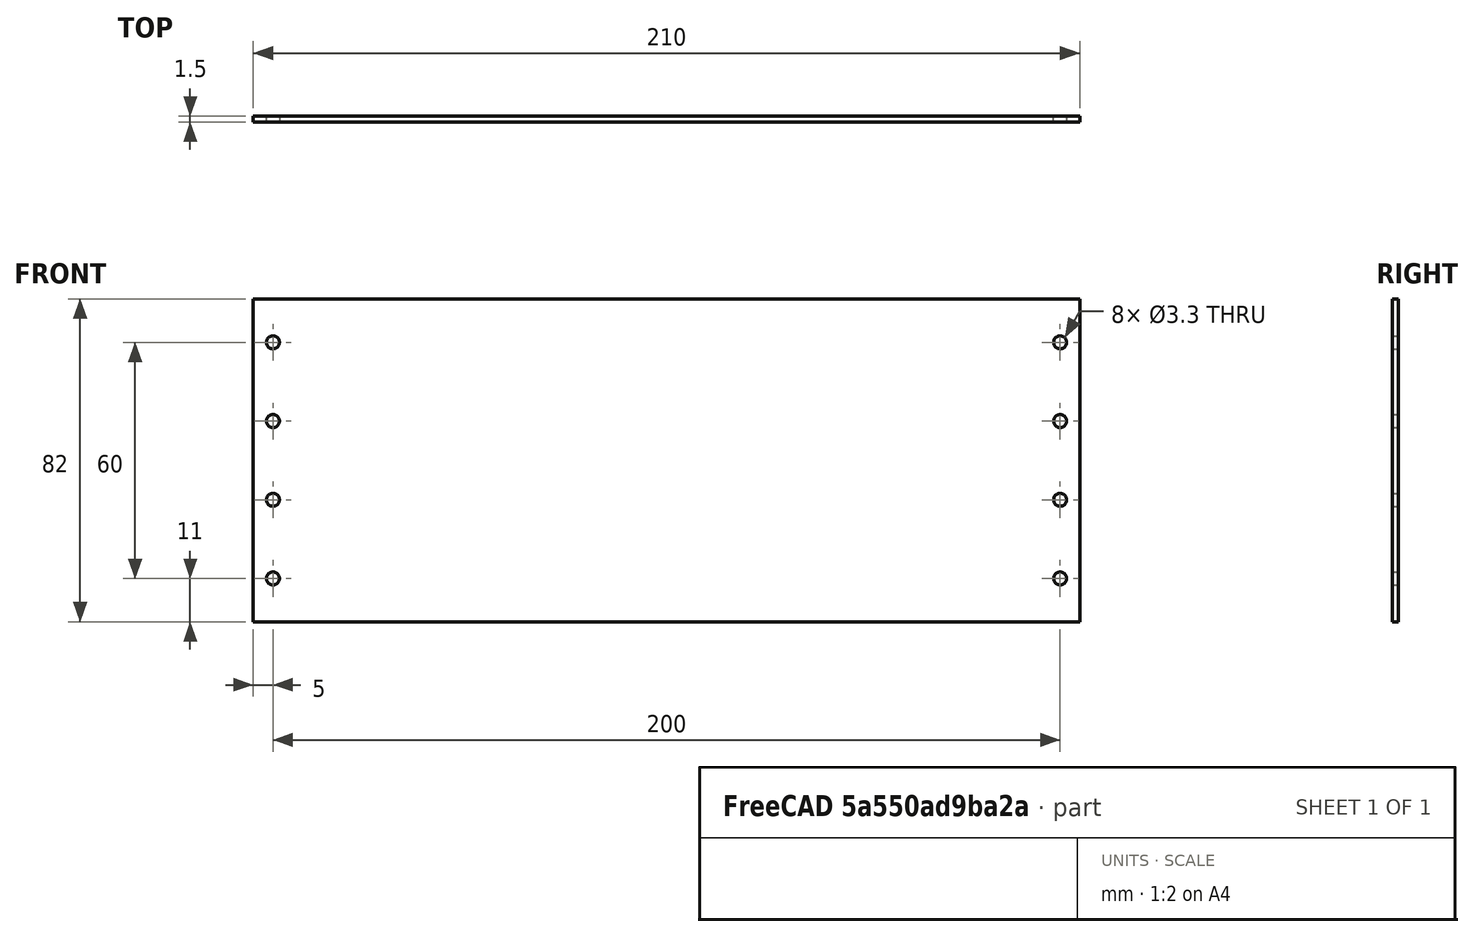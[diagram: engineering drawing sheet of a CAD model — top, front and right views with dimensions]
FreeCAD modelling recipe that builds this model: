
FCSTD DOCUMENT  (FreeCAD 1.0R39109 (Git))
Label: wall_lateral_template
License: All rights reserved
LicenseURL: https://en.wikipedia.org/wiki/All_rights_reserved
objects: Sketcher::SketchObject×2, PartDesign::Pad×1, PartDesign::Body×1
note: 8 computed .brp shape members not serialized (recipe doc carries the construction recipe); baked Part::Feature solids carry a one-line shape summary decoded from their .brp

FEATURE [Sketcher::SketchObject] Sketch
  ArcFitTolerance = 1e-06
  AttachmentSupport = -> [XZ_Plane]
  FullyConstrained = true
  MakeInternals = false
  MapMode = 5
  Placement = pos=(0,0,0) rot=(1,0,0;1.5708rad)
  sketch-geometry (18):
    g0: LineSegment StartX=-105 StartY=41 StartZ=0 EndX=-105 EndY=-41 EndZ=0
    g1: LineSegment StartX=-105 StartY=-41 StartZ=0 EndX=105 EndY=-41 EndZ=0
    g2: LineSegment StartX=105 StartY=-41 StartZ=0 EndX=105 EndY=41 EndZ=0
    g3: LineSegment StartX=105 StartY=41 StartZ=0 EndX=-105 EndY=41 EndZ=0
    g4: GeomPoint [constr] X=0 Y=0 Z=0
    g5: LineSegment [constr] StartX=-105 StartY=40 StartZ=0 EndX=-105 EndY=-40 EndZ=0
    g6: LineSegment [constr] StartX=-105 StartY=-40 StartZ=0 EndX=105 EndY=-40 EndZ=0
    g7: LineSegment [constr] StartX=105 StartY=-40 StartZ=0 EndX=105 EndY=40 EndZ=0
    g8: LineSegment [constr] StartX=105 StartY=40 StartZ=0 EndX=-105 EndY=40 EndZ=0
    g9: GeomPoint [constr] X=0 Y=0 Z=0
    g10: Circle CenterX=100 CenterY=30 CenterZ=0 NormalX=0 NormalY=0 NormalZ=1 AngleXU=0 Radius=1.65
    g11: Circle CenterX=100 CenterY=10 CenterZ=0 NormalX=0 NormalY=0 NormalZ=1 AngleXU=0 Radius=1.65
    g12: Circle CenterX=100 CenterY=-30 CenterZ=0 NormalX=0 NormalY=0 NormalZ=1 AngleXU=0 Radius=1.65
    g13: Circle CenterX=100 CenterY=-10 CenterZ=0 NormalX=0 NormalY=0 NormalZ=1 AngleXU=0 Radius=1.65
    g14: Circle CenterX=-100 CenterY=30 CenterZ=0 NormalX=0 NormalY=0 NormalZ=1 AngleXU=0 Radius=1.65
    g15: Circle CenterX=-100 CenterY=10 CenterZ=0 NormalX=0 NormalY=0 NormalZ=1 AngleXU=0 Radius=1.65
    g16: Circle CenterX=-100 CenterY=-30 CenterZ=0 NormalX=0 NormalY=0 NormalZ=1 AngleXU=0 Radius=1.65
    g17: Circle CenterX=-100 CenterY=-10 CenterZ=0 NormalX=0 NormalY=0 NormalZ=1 AngleXU=0 Radius=1.65
  constraints (42):
    c: Coincident(g0,g1)
    c: Coincident(g1,g2)
    c: Coincident(g2,g3)
    c: Coincident(g3,g0)
    c: Vertical(g0)
    c: Vertical(g2)
    c: Horizontal(g1)
    c: Horizontal(g3)
    c: Symmetric(g2,g0,g4)
    c: Coincident(g4,g-1)
    c: Coincident(g5,g6)
    c: Coincident(g6,g7)
    c: Coincident(g7,g8)
    c: Coincident(g8,g5)
    c: Vertical(g5)
    c: Vertical(g7)
    c: Horizontal(g6)
    c: Horizontal(g8)
    c: Symmetric(g7,g5,g9)
    c: Coincident(g9,g4)
    c: PointOnObject(g6,g2)
    c: DistanceY(g6,g7) = 80
    c: DistanceY(g1,g6) = 1
    c: DistanceX(g1,g1) = 210
    c: Equal(g10,g11)
    c: Radius(g11) = 1.65
    c: DistanceY(g11,g10) = 20
    c: Vertical(g10,g11)
    c: DistanceX(g10,g7) = 5
    c: DistanceY(g10,g7) = 10
    c: Equal(g12,g13)
    c: Radius(g13) = 1.65
    c: Equal(g14,g15)
    c: Radius(g15) = 1.65
    c: Equal(g16,g17)
    c: Radius(g17) = 1.65
    c: Symmetric(g10,g12,g-1)
    c: Symmetric(g13,g11,g-1)
    c: Symmetric(g12,g16,g-2)
    c: Symmetric(g17,g13,g-2)
    c: Symmetric(g11,g15,g-2)
    c: Symmetric(g14,g10,g-2)
FEATURE [PartDesign::Pad] Pad  label="BasePad"
  Direction = (0,-1,2e-16)
  Length = 0.75
  Length2 = 0.75
  Placement = pos=(0,0,0) rot=(1,0,0;1.5708rad)
  Profile = -> Sketch
  ReferenceAxis = -> Sketch [N_Axis]
  Refine = true
  Suppressed = false
  Type = 4
FEATURE [Sketcher::SketchObject] Sketch001
  ArcFitTolerance = 1e-06
  FullyConstrained = true
  MakeInternals = false
  MapMode = 5
  Placement = pos=(0,-1.5,0) rot=(1,0,0;1.5708rad)
FEATURE [PartDesign::Body] Body  label="wall_ldefault"
  AllowCompound = false
  Group = -> [Sketch,Pad,Sketch001]
  Origin = -> Origin
  Tip = -> Pad
